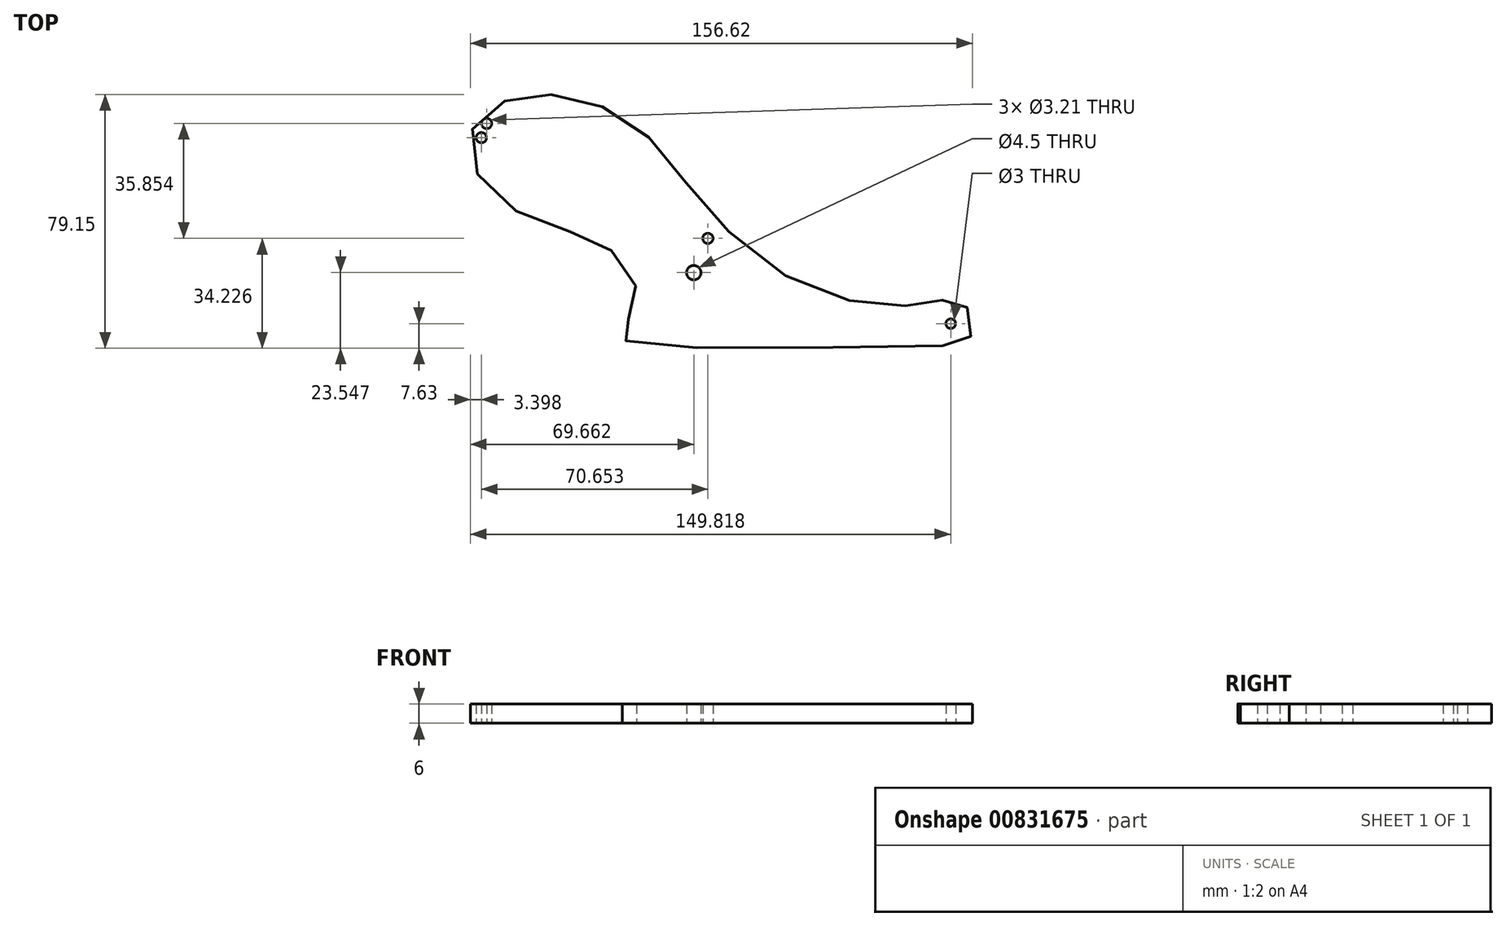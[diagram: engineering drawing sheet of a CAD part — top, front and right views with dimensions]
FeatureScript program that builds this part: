
annotation { "Feature Type Name" : "Feature", "Feature Type Description" : "" }
export const myFeature = defineFeature(function(context is Context, id is Id, definition is map)
    precondition{}
    {
        {
            var Q0;
            Q0=qCreatedBy(makeId("Top.planeOp"),FACE);
            var sketch = newSketch(context, id + "F0", { "sketchPlane" : qUnion([Q0])});
            skFitSpline(sketch, "E0", {"points": [v(105.51, 0) * mm, v(113.2, 1.1) * mm, v(114.8, 5.65) * mm, v(113.43, 11.35) * mm, v(109.79, 15.23) * mm, v(102.5, 13.17) * mm, v(92.7, 12.5) * mm, v(69.22, 15.9) * mm, v(40.96, 33.47) * mm, v(22.28, 54.88) * mm, v(7.7, 70.09) * mm, v(-11.27, 77.68) * mm, v(-25.9, 77.68) * mm, v(-38.91, 71.72) * mm, v(-41.62, 60.33) * mm, v(-34.04, 46.24) * mm, v(-13.44, 36.48) * mm, v(0, 31.06) * mm, v(8.78, 21.85) * mm, v(9.33, 11.55) * mm, v(6.5, 6.68) * mm, v(5.6, 2.92) * mm, v(13.51, 0) * mm, v(105.51, 0) * mm]});
            skCircle(sketch, "E1", {"center": v(-36.77, 69.32) * mm, "radius": 1.6 * mm});
            skCircle(sketch, "E2", {"center": v(-38.41, 64.9) * mm, "radius": 1.6 * mm});
            skCircle(sketch, "E3", {"center": v(32.24, 33.47) * mm, "radius": 1.6 * mm});
            skCircle(sketch, "E4", {"center": v(27.85, 22.79) * mm, "radius": 2.25 * mm});
            skCircle(sketch, "E5", {"center": v(108, 6.87) * mm, "radius": 1.5 * mm});
            skSolve(sketch);
        }
        {
            var Q0;
            Q0 = qSketchRegion(id + "F0", true);
            extrude(context, id + "F1", {"entities" : qUnion([Q0]), "depth" : 6 * mm, "offsetDistance" : 25 * mm});
        }
    });
